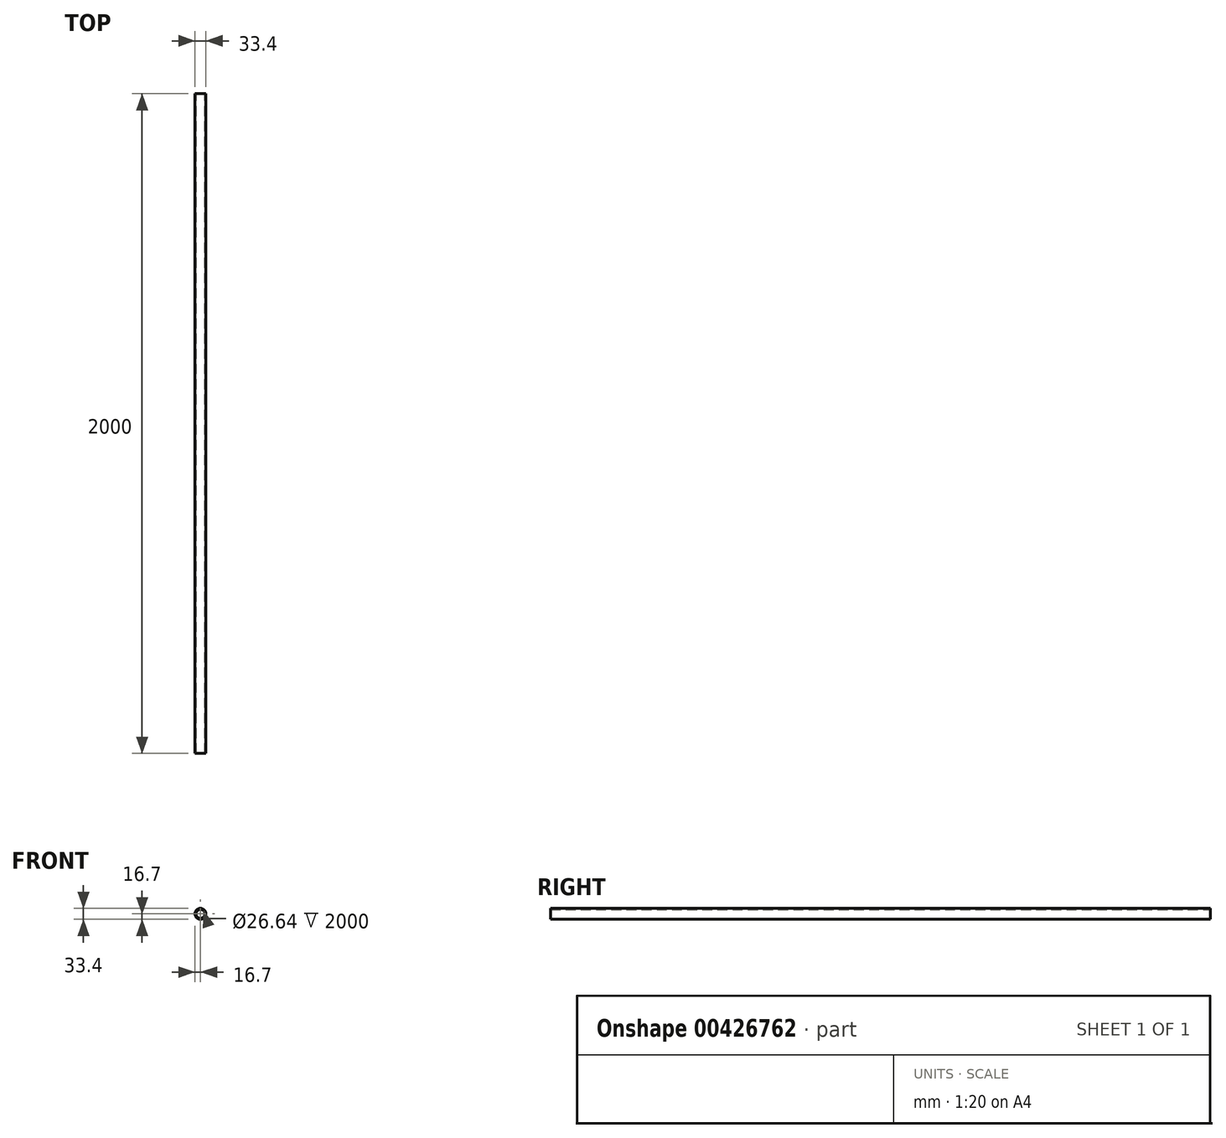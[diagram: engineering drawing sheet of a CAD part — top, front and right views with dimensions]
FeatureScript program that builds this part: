
annotation { "Feature Type Name" : "Feature", "Feature Type Description" : "" }
export const myFeature = defineFeature(function(context is Context, id is Id, definition is map)
    precondition{}
    {
        {
            var Q0;
            Q0=qCreatedBy(makeId("Front.planeOp"),FACE);
            var sketch = newSketch(context, id + "F0", { "sketchPlane" : qUnion([Q0])});
            skCircle(sketch, "E0", {"center": v(0, 0) * mm, "radius": 16.7 * mm});
            skCircle(sketch, "E1.0", {"center": v(0, 0) * mm, "radius": 13.32 * mm});
            skSolve(sketch);
        }
        {
            var Q0;
            Q0=makeQuery(id+"F0.imprint","IMPRINT",FACE,{"disambiguationData":[TD([[makeQuery(id+"F0.imprint","IMPRINT",EDGE,{"derivedFrom":sQuery(id+"F0.wireOp",EDGE,"E0")}),1.0]])]});
            extrude(context, id + "F1", {"entities" : qUnion([Q0]), "depth" : 2000 * mm});
        }
    });
